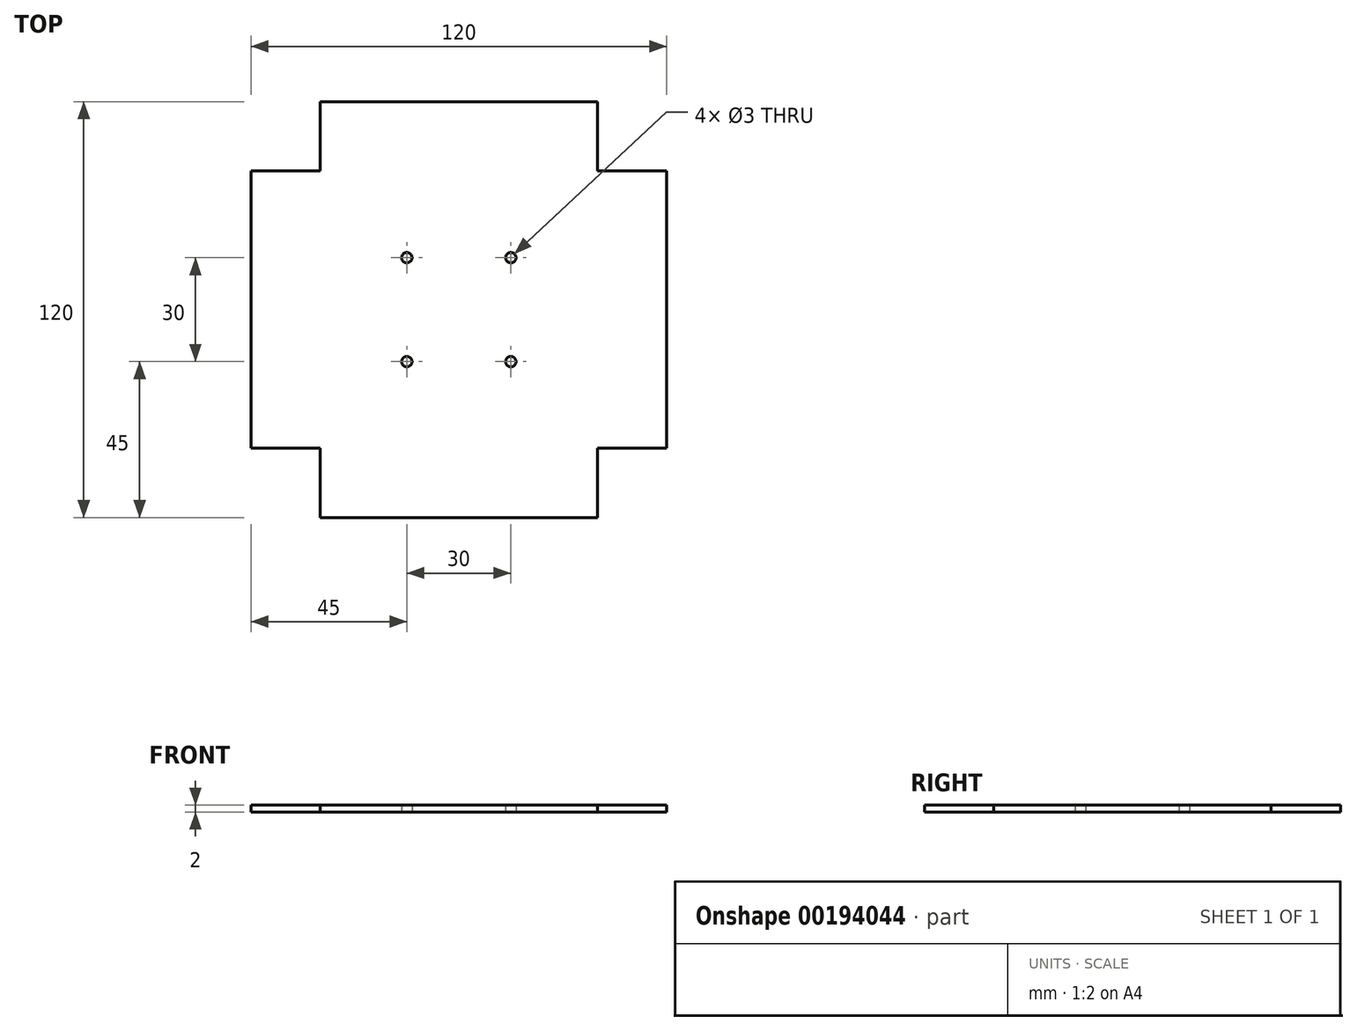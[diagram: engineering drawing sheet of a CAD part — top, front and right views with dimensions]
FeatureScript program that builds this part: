
annotation { "Feature Type Name" : "Feature", "Feature Type Description" : "" }
export const myFeature = defineFeature(function(context is Context, id is Id, definition is map)
    precondition{}
    {
        {
            var Q0;
            Q0=qCreatedBy(makeId("Top.planeOp"),FACE);
            var sketch = newSketch(context, id + "F0", { "sketchPlane" : qUnion([Q0])});
            skLineSegment(sketch, "E0", {"start": v(0, 60) * mm, "end": v(-40, 60) * mm});
            skLineSegment(sketch, "E1", {"start": v(-40, 60) * mm, "end": v(-40, 40) * mm});
            skLineSegment(sketch, "E2", {"start": v(-40, 40) * mm, "end": v(-60, 40) * mm});
            skLineSegment(sketch, "E3", {"start": v(-60, 40) * mm, "end": v(-60, 0) * mm});
            skLineSegment(sketch, "E4", {"start": v(-60, 0) * mm, "end": v(-60, -40) * mm});
            skLineSegment(sketch, "E5", {"start": v(-60, -40) * mm, "end": v(-40, -40) * mm});
            skLineSegment(sketch, "E6", {"start": v(-40, -40) * mm, "end": v(-40, -60) * mm});
            skLineSegment(sketch, "E7", {"start": v(-40, -60) * mm, "end": v(0, -60) * mm});
            skLineSegment(sketch, "E8", {"start": v(0, -60) * mm, "end": v(40, -60) * mm});
            skLineSegment(sketch, "E9", {"start": v(40, -60) * mm, "end": v(40, -40) * mm});
            skLineSegment(sketch, "E10", {"start": v(40, -40) * mm, "end": v(60, -40) * mm});
            skLineSegment(sketch, "E11", {"start": v(60, -40) * mm, "end": v(60, 0) * mm});
            skLineSegment(sketch, "E12", {"start": v(60, 0) * mm, "end": v(60, 40) * mm});
            skLineSegment(sketch, "E13", {"start": v(60, 40) * mm, "end": v(40, 40) * mm});
            skLineSegment(sketch, "E14", {"start": v(40, 40) * mm, "end": v(40, 60) * mm});
            skLineSegment(sketch, "E15", {"start": v(40, 60) * mm, "end": v(-4.43, 60) * mm});
            skSolve(sketch);
        }
        {
            var Q0;
            {var subQ0=sQuery(id+"F0.wireOp",EDGE,"E0");Q0=makeQuery(id+"F0.imprint","IMPRINT",FACE,{"disambiguationData":[TD([[makeQuery(id+"F0.imprint","IMPRINT",EDGE,{"derivedFrom":subQ0}),1.0]])]});}
            var sketch = newSketch(context, id + "F1", { "sketchPlane" : qUnion([Q0])});
            skCircle(sketch, "E16", {"center": v(-15, 15) * mm, "radius": 1.5 * mm});
            skCircle(sketch, "E17", {"center": v(-15, -15) * mm, "radius": 1.5 * mm});
            skCircle(sketch, "E18", {"center": v(15, 15) * mm, "radius": 1.5 * mm});
            skCircle(sketch, "E19", {"center": v(15, -15) * mm, "radius": 1.5 * mm});
            skSolve(sketch);
        }
        {
            var Q0;
            {var subQ0=sQuery(id+"F0.wireOp",EDGE,"E0");Q0=makeQuery(id+"F0.imprint","IMPRINT",FACE,{"disambiguationData":[TD([[makeQuery(id+"F0.imprint","IMPRINT",EDGE,{"derivedFrom":subQ0}),1.0]])]});}
            extrude(context, id + "F2", {"entities" : qUnion([Q0]), "depth" : 2 * mm});
        }
        {
            var Q0;
            Q0=sQuery(id+"F1.wireOp",VERTEX,"E16.center");
            var Q1;
            Q1=sQuery(id+"F1.wireOp",VERTEX,"E18.center");
            var Q2;
            Q2=sQuery(id+"F1.wireOp",VERTEX,"E17.center");
            var Q3;
            Q3=sQuery(id+"F1.wireOp",VERTEX,"E19.center");
            var Q4;
            Q4=makeQuery(id+"F2.opExtrude","SWEPT_BODY",BODY,{"disambiguationData":[OSD([sQuery(id+"F0.wireOp",EDGE,"E0"),sQuery(id+"F0.wireOp",EDGE,"E1"),sQuery(id+"F0.wireOp",EDGE,"E2"),sQuery(id+"F0.wireOp",EDGE,"E3"),sQuery(id+"F0.wireOp",EDGE,"E4"),sQuery(id+"F0.wireOp",EDGE,"E5"),sQuery(id+"F0.wireOp",EDGE,"E6"),sQuery(id+"F0.wireOp",EDGE,"E7"),sQuery(id+"F0.wireOp",EDGE,"E8"),sQuery(id+"F0.wireOp",EDGE,"E9"),sQuery(id+"F0.wireOp",EDGE,"E10"),sQuery(id+"F0.wireOp",EDGE,"E11"),sQuery(id+"F0.wireOp",EDGE,"E12"),sQuery(id+"F0.wireOp",EDGE,"E13"),sQuery(id+"F0.wireOp",EDGE,"E14"),sQuery(id+"F0.wireOp",EDGE,"E15")])]});
            hole(context, id + "F3", {"style" : HoleStyle.SIMPLE, "endStyle" : HoleEndStyle.THROUGH, "oppositeDirection" : true, "holeDiameter" : 3 * mm, "startFromSketch" : true, "locations" : qUnion([Q0, Q1, Q2, Q3]), "scope" : qUnion([Q4]), "isTappedThrough" : true});
        }
    });
